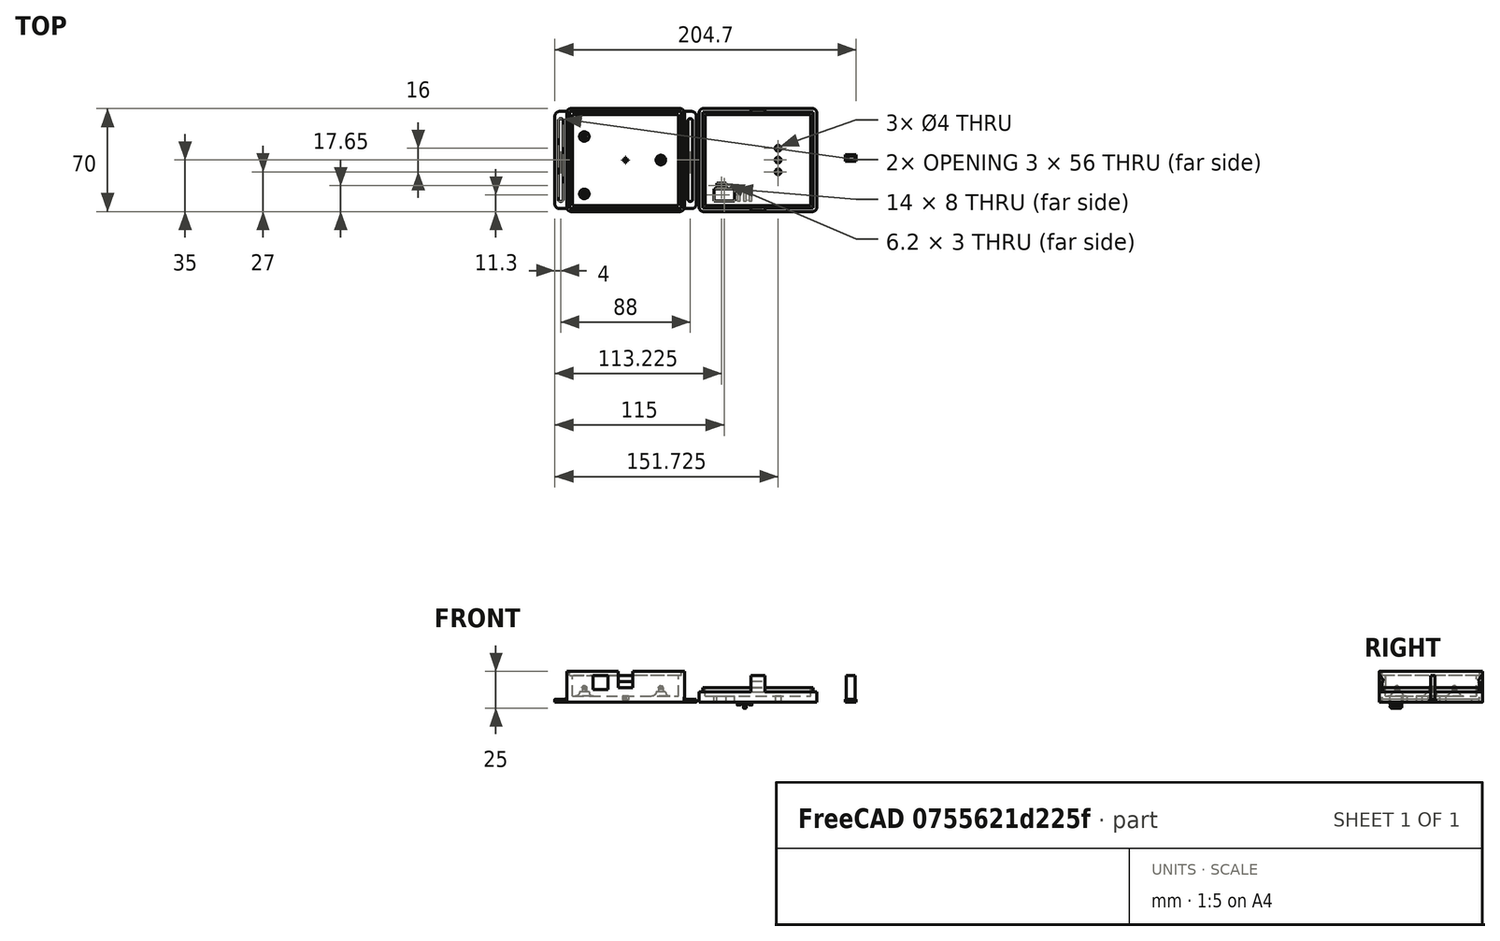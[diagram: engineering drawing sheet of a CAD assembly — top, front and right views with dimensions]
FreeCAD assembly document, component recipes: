
FREECAD ASSEMBLY — COMPONENT RECIPES ("case")

This assembly document has 3 components, labeled P0..P2 below (a component is one placed body or linked part). 3 of them carry a construction recipe — the FreeCAD feature program that regenerates the part from scratch, quoted from this document or its linked companion documents; the rest are supplied as boundary geometry only. No exploded tour is included for this assembly.
COMPONENT P0 — recipe-attached ("bottom_b001", modeled in this document).
Construction recipe (the document's own serialized feature program — sketch geometry with constraints, then the solid features built on it; lengths are millimeters unless a unit is written):

FEATURE [Sketcher::SketchObject] Sketch
  ArcFitTolerance = 1e-06
  AttachmentSupport = -> [XY_Plane001]
  FullyConstrained = true
  MakeInternals = false
  MapMode = 5
  sketch-geometry (4):
    g0: LineSegment StartX=-40 StartY=35 StartZ=0 EndX=-40 EndY=-35 EndZ=0
    g1: LineSegment StartX=-40 StartY=-35 StartZ=0 EndX=40 EndY=-35 EndZ=0
    g2: LineSegment StartX=40 StartY=-35 StartZ=0 EndX=40 EndY=35 EndZ=0
    g3: LineSegment StartX=40 StartY=35 StartZ=0 EndX=-40 EndY=35 EndZ=0
  constraints (10):
    c: Coincident(g0,g1)
    c: Coincident(g1,g2)
    c: Coincident(g2,g3)
    c: Coincident(g3,g0)
    c: Vertical(g2)
    c: Horizontal(g1)
    c: Symmetric(g0,g2,g-2)
    c: Symmetric(g0,g0,g-1)
    c: DistanceX(g3,g3) = 80
    c: DistanceY(g2,g2) = 70
FEATURE [PartDesign::Pad] Pad  label="case"
  Direction = (0,0,1)
  Length = 21
  Length2 = 10
  Profile = -> Sketch
  ReferenceAxis = -> Sketch [N_Axis]
  Refine = true
  Suppressed = false
  Type = 0
FEATURE [PartDesign::Thickness] Thickness  label="case_t"
  Base = -> Pad [Face6]
  BaseFeature = -> Pad
  Intersection = false
  Join = 0
  Mode = 0
  Refine = true
  Reversed = true
  SupportTransform = false
  Suppressed = false
  Value = 4
FEATURE [PartDesign::Fillet] Fillet
  Base = -> Thickness [Edge1,Edge2,Edge5,Edge8]
  BaseFeature = -> Thickness
  Radius = 3
  Refine = true
  SupportTransform = false
  Suppressed = false
  UseAllEdges = false
FEATURE [Sketcher::SketchObject] Sketch001  label="pcb_holders_s"
  ArcFitTolerance = 1e-06
  AttachmentSupport = -> [Fillet]
  FullyConstrained = true
  MakeInternals = false
  MapMode = 5
  Placement = pos=(0,0,4) rot=(0,0,1;0rad)
  sketch-geometry (7):
    g0: Circle CenterX=-28 CenterY=-23 CenterZ=0 NormalX=0 NormalY=0 NormalZ=1 AngleXU=0 Radius=3.25
    g1: Circle CenterX=-28 CenterY=16 CenterZ=0 NormalX=0 NormalY=0 NormalZ=1 AngleXU=0 Radius=3.25
    g2: Circle CenterX=24 CenterY=-1.1e-15 CenterZ=0 NormalX=0 NormalY=0 NormalZ=1 AngleXU=0 Radius=3.25
    g3: LineSegment [constr] StartX=-32 StartY=27 StartZ=0 EndX=-32 EndY=-27 EndZ=0
    g4: LineSegment [constr] StartX=-32 StartY=-27 StartZ=0 EndX=32 EndY=-27 EndZ=0
    g5: LineSegment [constr] StartX=32 StartY=-27 StartZ=0 EndX=32 EndY=27 EndZ=0
    g6: LineSegment [constr] StartX=32 StartY=27 StartZ=0 EndX=-32 EndY=27 EndZ=0
  constraints (19):
    c: Radius(g0) = 3.25
    c: Radius(g1) = 3.25
    c: Diameter(g2) = 6.5
    c: Coincident(g3,g4)
    c: Coincident(g4,g5)
    c: Coincident(g5,g6)
    c: Coincident(g6,g3)
    c: Vertical(g3)
    c: Horizontal(g6)
    c: DistanceX(g6,g6) = 64
    c: DistanceY(g3,g3) = 54
    c: Symmetric(g3,g4,g-2)
    c: Symmetric(g5,g4,g-1)
    c: Distance(g0,g4) = 4
    c: Distance(g0,g3) = 4
    c: Distance(g1,g3) = 4
    c: Distance(g1,g6) = 11
    c: Distance(g2,g5) = 8
    c: Distance(g2,g4) = 27
FEATURE [PartDesign::Pad] Pad001  label="pcb_holders_p"
  BaseFeature = -> Fillet
  Direction = (0,0,1)
  Length = 3
  Length2 = 10
  Profile = -> Sketch001
  ReferenceAxis = -> Sketch001 [N_Axis]
  Refine = true
  Suppressed = false
  Type = 0
FEATURE [PartDesign::Fillet] Fillet001  label="pcb_holder_f"
  Base = -> Pad001 [Edge39,Edge38,Edge37]
  BaseFeature = -> Pad001
  Radius = 2.99
  Refine = true
  SupportTransform = false
  Suppressed = false
  UseAllEdges = false
FEATURE [Sketcher::SketchObject] Sketch003  label="barreljack_window_s"
  ArcFitTolerance = 1e-06
  AttachmentOffset = pos=(0,0,8.55) rot=(0,0,1;0rad)
  AttachmentSupport = -> [XY_Plane001]
  FullyConstrained = true
  MakeInternals = false
  MapMode = 5
  Placement = pos=(0,0,8.55) rot=(0,0,1;0rad)
  sketch-geometry (8):
    g0: LineSegment [constr] StartX=-32 StartY=27 StartZ=0 EndX=-32 EndY=-27 EndZ=0
    g1: LineSegment [constr] StartX=-32 StartY=-27 StartZ=0 EndX=32 EndY=-27 EndZ=0
    g2: LineSegment [constr] StartX=32 StartY=-27 StartZ=0 EndX=32 EndY=27 EndZ=0
    g3: LineSegment [constr] StartX=32 StartY=27 StartZ=0 EndX=-32 EndY=27 EndZ=0
    g4: LineSegment StartX=-22 StartY=-20 StartZ=0 EndX=-22 EndY=-36 EndZ=0
    g5: LineSegment StartX=-22 StartY=-36 StartZ=0 EndX=-12 EndY=-36 EndZ=0
    g6: LineSegment StartX=-12 StartY=-36 StartZ=0 EndX=-12 EndY=-20 EndZ=0
    g7: LineSegment StartX=-12 StartY=-20 StartZ=0 EndX=-22 EndY=-20 EndZ=0
  constraints (22):
    c: Coincident(g0,g1)
    c: Coincident(g1,g2)
    c: Coincident(g2,g3)
    c: Coincident(g3,g0)
    c: Vertical(g2)
    c: Horizontal(g1)
    c: Distance(g0,g2) = 64
    c: Distance(g1,g3) = 54
    c: Symmetric(g0,g2,g-2)
    c: Symmetric(g0,g0,g-1)
    c: Coincident(g4,g5)
    c: Coincident(g5,g6)
    c: Coincident(g6,g7)
    c: Coincident(g7,g4)
    c: Vertical(g4)
    c: Vertical(g6)
    c: Horizontal(g5)
    c: Horizontal(g7)
    c: Distance(g0,g4) = 10
    c: DistanceX(g7,g7) = 10
    c: DistanceY(g6,g6) = 16
    c: Distance(g1,g7) = 7
FEATURE [PartDesign::Pocket] Pocket  label="barreljack_window_p"
  BaseFeature = -> Fillet001
  Direction = (0,0,-1)
  Length = 9.5
  Length2 = 5
  Profile = -> Sketch003
  ReferenceAxis = -> Sketch003 [N_Axis]
  Refine = true
  Reversed = true
  Suppressed = false
  Type = 0
FEATURE [Sketcher::SketchObject] Sketch004  label="fitting_s001"
  ArcFitTolerance = 1e-06
  AttachmentOffset = pos=(0,0,18) rot=(0,0,1;0rad)
  AttachmentSupport = -> [XY_Plane001]
  ExternalGeometry = -> [Pocket]
  FullyConstrained = true
  MakeInternals = false
  MapMode = 5
  Placement = pos=(0,0,18) rot=(0,0,1;0rad)
  sketch-geometry (4):
    g0: LineSegment StartX=-38 StartY=33 StartZ=0 EndX=-38 EndY=-33 EndZ=0
    g1: LineSegment StartX=-38 StartY=-33 StartZ=0 EndX=38 EndY=-33 EndZ=0
    g2: LineSegment StartX=38 StartY=-33 StartZ=0 EndX=38 EndY=33 EndZ=0
    g3: LineSegment StartX=38 StartY=33 StartZ=0 EndX=-38 EndY=33 EndZ=0
  constraints (12):
    c: Coincident(g0,g1)
    c: Coincident(g1,g2)
    c: Coincident(g2,g3)
    c: Coincident(g3,g0)
    c: Vertical(g0)
    c: Vertical(g2)
    c: Horizontal(g1)
    c: Horizontal(g3)
    c: DistanceX(g0,g-4) = 2
    c: DistanceY(g-4,g0) = 2
    c: DistanceY(g1,g-6) = 2
    c: DistanceX(g-6,g1) = 2
FEATURE [PartDesign::Pocket] Pocket001  label="fitting_p001"
  BaseFeature = -> Pocket
  Direction = (0,0,-1)
  Length = 5
  Length2 = 5
  Profile = -> Sketch004
  ReferenceAxis = -> Sketch004 [N_Axis]
  Refine = true
  Reversed = true
  Suppressed = false
  Type = 0
FEATURE [Sketcher::SketchObject] Sketch018  label="holders_s"
  ArcFitTolerance = 1e-06
  AttachmentSupport = -> [XY_Plane001]
  FullyConstrained = true
  MakeInternals = false
  MapMode = 5
  sketch-geometry (40):
    g0: LineSegment StartX=-38 StartY=33 StartZ=0 EndX=-45 EndY=33 EndZ=0
    g1: LineSegment StartX=-48 StartY=30 StartZ=0 EndX=-48 EndY=-30 EndZ=0
    g2: LineSegment StartX=-45 StartY=-33 StartZ=0 EndX=-38 EndY=-33 EndZ=0
    g3: LineSegment StartX=-38 StartY=-33 StartZ=0 EndX=-38 EndY=33 EndZ=0
    g4: LineSegment StartX=38 StartY=33 StartZ=0 EndX=38 EndY=-33 EndZ=0
    g5: LineSegment StartX=38 StartY=-33 StartZ=0 EndX=45 EndY=-33 EndZ=0
    g6: LineSegment StartX=48 StartY=-30 StartZ=0 EndX=48 EndY=30 EndZ=0
    g7: LineSegment StartX=45 StartY=33 StartZ=0 EndX=38 EndY=33 EndZ=0
    g8: ArcOfCircle CenterX=-45 CenterY=30 CenterZ=0 NormalX=0 NormalY=0 NormalZ=1 AngleXU=0 Radius=3 StartAngle=1.5708 EndAngle=3.14159
    g9: GeomPoint [constr] X=-48 Y=33 Z=0
    g10: ArcOfCircle CenterX=-45 CenterY=-30 CenterZ=0 NormalX=0 NormalY=0 NormalZ=1 AngleXU=0 Radius=3 StartAngle=3.14159 EndAngle=4.71239
    g11: GeomPoint [constr] X=-48 Y=-33 Z=0
    g12: ArcOfCircle CenterX=45 CenterY=30 CenterZ=0 NormalX=0 NormalY=0 NormalZ=1 AngleXU=0 Radius=3 StartAngle=2e-16 EndAngle=1.5708
    g13: GeomPoint [constr] X=48 Y=33 Z=0
    g14: ArcOfCircle CenterX=45 CenterY=-30 CenterZ=0 NormalX=0 NormalY=0 NormalZ=1 AngleXU=0 Radius=3 StartAngle=4.71239 EndAngle=6.28319
    g15: GeomPoint [constr] X=48 Y=-33 Z=0
    g16: LineSegment StartX=-45.5 StartY=27 StartZ=0 EndX=-45.5 EndY=-27 EndZ=0
    g17: LineSegment StartX=-44.5 StartY=-28 StartZ=0 EndX=-43.5 EndY=-28 EndZ=0
    g18: LineSegment StartX=-42.5 StartY=-27 StartZ=0 EndX=-42.5 EndY=27 EndZ=0
    g19: LineSegment StartX=-43.5 StartY=28 StartZ=0 EndX=-44.5 EndY=28 EndZ=0
    g20: LineSegment StartX=42.5 StartY=27 StartZ=0 EndX=42.5 EndY=-27 EndZ=0
    g21: LineSegment StartX=43.5 StartY=-28 StartZ=0 EndX=44.5 EndY=-28 EndZ=0
    g22: LineSegment StartX=45.5 StartY=-27 StartZ=0 EndX=45.5 EndY=27 EndZ=0
    g23: LineSegment StartX=44.5 StartY=28 StartZ=0 EndX=43.5 EndY=28 EndZ=0
    g24: ArcOfCircle CenterX=-44.5 CenterY=27 CenterZ=0 NormalX=0 NormalY=0 NormalZ=1 AngleXU=0 Radius=1 StartAngle=1.5708 EndAngle=3.14159
    g25: GeomPoint [constr] X=-45.5 Y=28 Z=0
    g26: ArcOfCircle CenterX=-43.5 CenterY=27 CenterZ=0 NormalX=0 NormalY=0 NormalZ=1 AngleXU=0 Radius=1 StartAngle=1.7e-15 EndAngle=1.5708
    g27: GeomPoint [constr] X=-42.5 Y=28 Z=0
    g28: ArcOfCircle CenterX=-44.5 CenterY=-27 CenterZ=0 NormalX=0 NormalY=0 NormalZ=1 AngleXU=0 Radius=1 StartAngle=3.14159 EndAngle=4.71239
    g29: GeomPoint [constr] X=-45.5 Y=-28 Z=0
    g30: ArcOfCircle CenterX=-43.5 CenterY=-27 CenterZ=0 NormalX=0 NormalY=0 NormalZ=1 AngleXU=0 Radius=1 StartAngle=4.71239 EndAngle=6.28319
    g31: GeomPoint [constr] X=-42.5 Y=-28 Z=0
    g32: ArcOfCircle CenterX=43.5 CenterY=-27 CenterZ=0 NormalX=0 NormalY=0 NormalZ=1 AngleXU=0 Radius=1 StartAngle=3.14159 EndAngle=4.71239
    g33: GeomPoint [constr] X=42.5 Y=-28 Z=0
    g34: ArcOfCircle CenterX=44.5 CenterY=-27 CenterZ=0 NormalX=0 NormalY=0 NormalZ=1 AngleXU=0 Radius=1 StartAngle=4.71239 EndAngle=6.28319
    g35: GeomPoint [constr] X=45.5 Y=-28 Z=0
    g36: ArcOfCircle CenterX=43.5 CenterY=27 CenterZ=0 NormalX=0 NormalY=0 NormalZ=1 AngleXU=0 Radius=1 StartAngle=1.5708 EndAngle=3.14159
    g37: GeomPoint [constr] X=42.5 Y=28 Z=0
    g38: ArcOfCircle CenterX=44.5 CenterY=27 CenterZ=0 NormalX=0 NormalY=0 NormalZ=1 AngleXU=0 Radius=1 StartAngle=-5.7785e-12 EndAngle=1.5708
    g39: GeomPoint [constr] X=45.5 Y=28 Z=0
  constraints (94):
    c: Coincident(g2,g3)
    c: Coincident(g3,g0)
    c: Horizontal(g0)
    c: Horizontal(g2)
    c: Vertical(g1)
    c: Vertical(g3)
    c: Distance(g9,g3) = 10
    c: Distance(g0,g2) = 66
    c: Coincident(g0,g-3)
    c: Coincident(g4,g5)
    c: Coincident(g7,g4)
    c: Vertical(g4)
    c: Vertical(g6)
    c: Horizontal(g5)
    c: Horizontal(g7)
    c: Distance(g4,g13) = 10
    c: Distance(g5,g7) = 66
    c: Coincident(g4,g-4)
    c: PointOnObject(g9,g0)
    c: PointOnObject(g9,g1)
    c: Tangent(g0,g8) = -1.5708
    c: Tangent(g1,g8) = -1.5708
    c: PointOnObject(g11,g1)
    c: PointOnObject(g11,g2)
    c: Tangent(g1,g10) = -1.5708
    c: Tangent(g2,g10) = -1.5708
    c: PointOnObject(g13,g7)
    c: PointOnObject(g13,g6)
    c: Tangent(g7,g12) = -1.5708
    c: Tangent(g6,g12) = -1.5708
    c: PointOnObject(g15,g5)
    c: PointOnObject(g15,g6)
    c: Tangent(g5,g14) = -1.5708
    c: Tangent(g6,g14) = -1.5708
    c: Radius(g8) = 3
    c: Radius(g10) = 3
    c: Radius(g14) = 3
    c: Radius(g12) = 3
    c: Vertical(g16)
    c: Vertical(g18)
    c: Horizontal(g17)
    c: Horizontal(g19)
    c: Distance(g25,g27) = 3
    c: Distance(g29,g25) = 56
    c: Distance(g3,g18) = 4.5
    c: Vertical(g20)
    c: Vertical(g22)
    c: Horizontal(g21)
    c: Horizontal(g23)
    c: Distance(g37,g39) = 3
    c: Distance(g33,g37) = 56
    c: Distance(g4,g20) = 4.5
    c: Distance(g27,g0) = 5
    c: Distance(g39,g7) = 5
    c: PointOnObject(g25,g19)
    c: PointOnObject(g25,g16)
    c: Tangent(g19,g24) = -1.5708
    c: Tangent(g16,g24) = -1.5708
    c: PointOnObject(g27,g19)
    c: PointOnObject(g27,g18)
    c: Tangent(g19,g26) = -1.5708
    c: Tangent(g18,g26) = -1.5708
    c: PointOnObject(g29,g17)
    c: PointOnObject(g29,g16)
    c: Tangent(g17,g28) = -1.5708
    c: Tangent(g16,g28) = -1.5708
    c: PointOnObject(g31,g17)
    c: PointOnObject(g31,g18)
    c: Tangent(g17,g30) = -1.5708
    c: Tangent(g18,g30) = -1.5708
    c: PointOnObject(g33,g20)
    c: PointOnObject(g33,g21)
    c: Tangent(g20,g32) = -1.5708
    c: Tangent(g21,g32) = -1.5708
    c: PointOnObject(g35,g22)
    c: PointOnObject(g35,g21)
    c: Tangent(g22,g34) = -1.5708
    c: Tangent(g21,g34) = -1.5708
    c: PointOnObject(g37,g23)
    c: PointOnObject(g37,g20)
    c: Tangent(g23,g36) = -1.5708
    c: Tangent(g20,g36) = -1.5708
    c: PointOnObject(g39,g23)
    c: PointOnObject(g39,g22)
    c: Tangent(g23,g38) = -1.5708
    c: Tangent(g22,g38) = -1.5708
    c: Radius(g24) = 1
    c: Radius(g26) = 1
    c: Radius(g28) = 1
    c: Radius(g30) = 1
    c: Radius(g32) = 1
    c: Radius(g34) = 1
    c: Radius(g36) = 1
    c: Radius(g38) = 1
FEATURE [PartDesign::Pad] Pad009  label="holders_p"
  BaseFeature = -> Pocket001
  Direction = (0,0,1)
  Length = 2
  Length2 = 10
  Profile = -> Sketch018
  ReferenceAxis = -> Sketch018 [N_Axis]
  Refine = true
  Suppressed = false
  Type = 0
FEATURE [PartDesign::Fillet] Fillet004  label="holders_f"
  Base = -> Pad009 [Edge77,Edge89]
  BaseFeature = -> Pad009
  Radius = 1.5
  Refine = true
  SupportTransform = false
  Suppressed = false
  UseAllEdges = false
FEATURE [Sketcher::SketchObject] Sketch016  label="clips_holders_s"
  ArcFitTolerance = 1e-06
  AttachmentSupport = -> [YZ_Plane001]
  ExternalGeometry = -> [Pad]
  FullyConstrained = true
  MakeInternals = false
  MapMode = 5
  Placement = pos=(0,0,0) rot=(0.57735,0.57735,0.57735;2.0944rad)
  sketch-geometry (10):
    g0: LineSegment StartX=33 StartY=18 StartZ=0 EndX=35 EndY=18 EndZ=0
    g1: LineSegment StartX=35 StartY=18 StartZ=0 EndX=35 EndY=9.9 EndZ=0
    g2: LineSegment StartX=35 StartY=9.9 StartZ=0 EndX=31.9 EndY=14.1 EndZ=0
    g3: LineSegment StartX=31.9 StartY=14.1 StartZ=0 EndX=33 EndY=14.1 EndZ=0
    g4: LineSegment StartX=33 StartY=14.1 StartZ=0 EndX=33 EndY=18 EndZ=0
    g5: LineSegment StartX=-33 StartY=18 StartZ=0 EndX=-35 EndY=18 EndZ=0
    g6: LineSegment StartX=-35 StartY=18 StartZ=0 EndX=-35 EndY=9.9 EndZ=0
    g7: LineSegment StartX=-35 StartY=9.9 StartZ=0 EndX=-31.9 EndY=14.1 EndZ=0
    g8: LineSegment StartX=-31.9 StartY=14.1 StartZ=0 EndX=-33 EndY=14.1 EndZ=0
    g9: LineSegment StartX=-33 StartY=14.1 StartZ=0 EndX=-33 EndY=18 EndZ=0
  constraints (30):
    c: Coincident(g0,g1)
    c: Vertical(g1)
    c: Coincident(g2,g3)
    c: Coincident(g3,g4)
    c: Coincident(g4,g0)
    c: Vertical(g4)
    c: Coincident(g7,g8)
    c: Coincident(g8,g9)
    c: Coincident(g9,g5)
    c: Horizontal(g5)
    c: Coincident(g6,g5)
    c: DistanceY(g6,g6) = 8.1
    c: DistanceY(g9,g9) = 3.9
    c: Vertical(g9)
    c: Horizontal(g8)
    c: Vertical(g6)
    c: DistanceX(g8,g8) = 1.1
    c: DistanceY(g1,g1) = 8.1
    c: Horizontal(g3)
    c: DistanceX(g0,g0) = 2
    c: DistanceY(g4,g4) = 3.9
    c: DistanceX(g3,g3) = 1.1
    c: Horizontal(g0)
    c: DistanceX(g5,g5) = 2
    c: DistanceY(g5,g-3) = 3
    c: PointOnObject(g5,g-4)
    c: DistanceY(g0,g-5) = 3
    c: PointOnObject(g0,g-5)
    c: Coincident(g2,g1)
    c: Coincident(g7,g6)
FEATURE [PartDesign::Pocket] Pocket007  label="clip_holders_p"
  BaseFeature = -> Fillet004
  Direction = (-1,0,0)
  Length = 10
  Length2 = 5
  Midplane = true
  Profile = -> Sketch016
  ReferenceAxis = -> Sketch016 [N_Axis]
  Refine = true
  Suppressed = false
  Type = 0
FEATURE [Sketcher::SketchObject] Sketch019  label="clip_holders_clearance_s"
  ArcFitTolerance = 1e-06
  AttachmentSupport = -> [YZ_Plane001]
  ExternalGeometry = -> [Pocket007]
  FullyConstrained = true
  MakeInternals = false
  MapMode = 5
  Placement = pos=(0,0,0) rot=(0.57735,0.57735,0.57735;2.0944rad)
  sketch-geometry (8):
    g0: LineSegment StartX=-33 StartY=21 StartZ=0 EndX=-35 EndY=21 EndZ=0
    g1: LineSegment StartX=-35 StartY=21 StartZ=0 EndX=-35 EndY=18 EndZ=0
    g2: LineSegment StartX=-35 StartY=18 StartZ=0 EndX=-33 EndY=18 EndZ=0
    g3: LineSegment StartX=-33 StartY=18 StartZ=0 EndX=-33 EndY=21 EndZ=0
    g4: LineSegment StartX=33 StartY=21 StartZ=0 EndX=33 EndY=18 EndZ=0
    g5: LineSegment StartX=33 StartY=18 StartZ=0 EndX=35 EndY=18 EndZ=0
    g6: LineSegment StartX=35 StartY=18 StartZ=0 EndX=35 EndY=21 EndZ=0
    g7: LineSegment StartX=35 StartY=21 StartZ=0 EndX=33 EndY=21 EndZ=0
  constraints (20):
    c: Coincident(g0,g1)
    c: Coincident(g1,g2)
    c: Coincident(g2,g3)
    c: Coincident(g3,g0)
    c: Horizontal(g0)
    c: Horizontal(g2)
    c: Vertical(g1)
    c: Vertical(g3)
    c: Coincident(g0,g-5)
    c: Coincident(g1,g-6)
    c: Coincident(g4,g5)
    c: Coincident(g5,g6)
    c: Coincident(g6,g7)
    c: Coincident(g7,g4)
    c: Vertical(g4)
    c: Vertical(g6)
    c: Horizontal(g5)
    c: Horizontal(g7)
    c: Coincident(g4,g-10)
    c: Coincident(g5,g-9)
FEATURE [PartDesign::Pocket] Pocket008  label="clip_holder_clearance_p"
  BaseFeature = -> Pocket007
  Direction = (-1,0,0)
  Length = 10
  Length2 = 5
  Midplane = true
  Profile = -> Sketch019
  ReferenceAxis = -> Sketch019 [N_Axis]
  Refine = true
  Suppressed = false
  Type = 0
FEATURE [PartDesign::Boolean] Boolean006
  BaseFeature = -> Pocket008
  Group = -> [Body005]
  Refine = true
  Suppressed = false
  Type = 0
  UsePlacement = true
FEATURE [PartDesign::Boolean] Boolean007
  BaseFeature = -> Boolean006
  Group = -> [Body008,Body011]
  Refine = true
  Suppressed = false
  Type = 0
  UsePlacement = true
FEATURE [PartDesign::Body] Body  label="bottom_b"
  AllowCompound = false
  Group = -> [Sketch,Pad,Thickness,Fillet,Sketch001,Pad001,Fillet001,Sketch003,Pocket,Sketch004,Pocket001,Sketch016,Sketch018,Pad009,Fillet004,Pocket007,Sketch019,Pocket008,Boolean006,Boolean007]
  Origin = -> Origin001
  Tip = -> Boolean007
COMPONENT P1 — recipe-attached ("button_b001", modeled in this document).
Construction recipe (the document's own serialized feature program — sketch geometry with constraints, then the solid features built on it; lengths are millimeters unless a unit is written):

FEATURE [Sketcher::SketchObject] Sketch014
  ArcFitTolerance = 1e-06
  AttachmentSupport = -> [XY_Plane005]
  FullyConstrained = true
  MakeInternals = false
  MapMode = 5
  sketch-geometry (4):
    g0: LineSegment StartX=0 StartY=2.7 StartZ=0 EndX=0 EndY=0 EndZ=0
    g1: LineSegment StartX=0 StartY=0 StartZ=0 EndX=5.9 EndY=0 EndZ=0
    g2: LineSegment StartX=5.9 StartY=0 StartZ=0 EndX=5.9 EndY=2.7 EndZ=0
    g3: LineSegment StartX=5.9 StartY=2.7 StartZ=0 EndX=0 EndY=2.7 EndZ=0
  constraints (11):
    c: Coincident(g0,g1)
    c: Coincident(g1,g2)
    c: Coincident(g2,g3)
    c: Coincident(g3,g0)
    c: Vertical(g0)
    c: Vertical(g2)
    c: Horizontal(g1)
    c: Horizontal(g3)
    c: Distance(g0,g2) = 5.9
    c: Distance(g1,g3) = 2.7
    c: Coincident(g0,g-1)
FEATURE [PartDesign::Pad] Pad006
  Direction = (0,0,1)
  Length = 18
  Length2 = 10
  Profile = -> Sketch014
  ReferenceAxis = -> Sketch014 [N_Axis]
  Refine = true
  Suppressed = false
  Type = 0
FEATURE [Sketcher::SketchObject] Sketch015
  ArcFitTolerance = 1e-06
  AttachmentSupport = -> [XY_Plane005]
  ExternalGeometry = -> [Sketch014]
  FullyConstrained = true
  MakeInternals = false
  MapMode = 5
  sketch-geometry (4):
    g0: LineSegment StartX=-0.8 StartY=3.5 StartZ=0 EndX=-0.8 EndY=-0.8 EndZ=0
    g1: LineSegment StartX=-0.8 StartY=-0.8 StartZ=0 EndX=6.7 EndY=-0.8 EndZ=0
    g2: LineSegment StartX=6.7 StartY=-0.8 StartZ=0 EndX=6.7 EndY=3.5 EndZ=0
    g3: LineSegment StartX=6.7 StartY=3.5 StartZ=0 EndX=-0.8 EndY=3.5 EndZ=0
  constraints (12):
    c: Coincident(g0,g1)
    c: Coincident(g1,g2)
    c: Coincident(g2,g3)
    c: Coincident(g3,g0)
    c: Vertical(g0)
    c: Vertical(g2)
    c: Horizontal(g1)
    c: Horizontal(g3)
    c: Distance(g-3,g3) = 0.8
    c: Distance(g2,g-4) = 0.8
    c: Distance(g-3,g0) = 0.8
    c: Distance(g-4,g1) = 0.8
FEATURE [PartDesign::Pad] Pad007
  BaseFeature = -> Pad006
  Direction = (0,0,1)
  Length = 2
  Length2 = 10
  Profile = -> Sketch015
  ReferenceAxis = -> Sketch015 [N_Axis]
  Refine = true
  Suppressed = false
  Type = 0
FEATURE [PartDesign::Body] Body004  label="button_b"
  AllowCompound = false
  Group = -> [Sketch014,Pad006,Sketch015,Pad007]
  Origin = -> Origin005
  Placement = pos=(150,0,0) rot=(0,0,1;0rad)
  Tip = -> Pad007
COMPONENT P2 — recipe-attached ("top_b001", modeled in this document).
Construction recipe (the document's own serialized feature program — sketch geometry with constraints, then the solid features built on it; lengths are millimeters unless a unit is written):

FEATURE [Sketcher::SketchObject] Sketch005  label="case_s"
  ArcFitTolerance = 1e-06
  AttachmentSupport = -> [XY_Plane002]
  FullyConstrained = true
  MakeInternals = false
  MapMode = 5
  sketch-geometry (4):
    g0: LineSegment StartX=-40 StartY=35 StartZ=0 EndX=-40 EndY=-35 EndZ=0
    g1: LineSegment StartX=-40 StartY=-35 StartZ=0 EndX=40 EndY=-35 EndZ=0
    g2: LineSegment StartX=40 StartY=-35 StartZ=0 EndX=40 EndY=35 EndZ=0
    g3: LineSegment StartX=40 StartY=35 StartZ=0 EndX=-40 EndY=35 EndZ=0
  constraints (10):
    c: Coincident(g0,g1)
    c: Coincident(g1,g2)
    c: Coincident(g2,g3)
    c: Coincident(g3,g0)
    c: Vertical(g2)
    c: Horizontal(g1)
    c: Symmetric(g0,g2,g-2)
    c: Symmetric(g0,g0,g-1)
    c: DistanceX(g3,g3) = 80
    c: DistanceY(g2,g2) = 70
FEATURE [PartDesign::Pad] Pad003  label="case_p"
  Direction = (0,0,1)
  Length = 10
  Length2 = 10
  Profile = -> Sketch005
  ReferenceAxis = -> Sketch005 [N_Axis]
  Refine = true
  Suppressed = false
  Type = 0
FEATURE [PartDesign::Thickness] Thickness001  label="case_t001"
  Base = -> Pad003 [Face6]
  BaseFeature = -> Pad003
  Intersection = false
  Join = 0
  Mode = 0
  Refine = true
  Reversed = true
  SupportTransform = false
  Suppressed = false
  Value = 4
FEATURE [PartDesign::Fillet] Fillet002
  Base = -> Thickness001 [Edge2,Edge1,Edge5,Edge8]
  BaseFeature = -> Thickness001
  Radius = 3
  Refine = true
  SupportTransform = false
  Suppressed = false
  UseAllEdges = false
FEATURE [Sketcher::SketchObject] Sketch008  label="fitting_s"
  ArcFitTolerance = 1e-06
  AttachmentOffset = pos=(0,0,7) rot=(0,0,1;0rad)
  AttachmentSupport = -> [XY_Plane002]
  FullyConstrained = true
  MakeInternals = false
  MapMode = 5
  Placement = pos=(0,0,7) rot=(0,0,1;0rad)
  sketch-geometry (20):
    g0: LineSegment StartX=-42.5 StartY=50 StartZ=0 EndX=-42.5 EndY=-50 EndZ=0
    g1: LineSegment StartX=-42.5 StartY=-50 StartZ=0 EndX=-37.5 EndY=-50 EndZ=0
    g2: LineSegment StartX=-37.5 StartY=-50 StartZ=0 EndX=-37.5 EndY=50 EndZ=0
    g3: LineSegment StartX=-37.5 StartY=50 StartZ=0 EndX=-42.5 EndY=50 EndZ=0
    g4: LineSegment StartX=-50 StartY=37.5 StartZ=0 EndX=-50 EndY=32.5 EndZ=0
    g5: LineSegment StartX=-50 StartY=32.5 StartZ=0 EndX=50 EndY=32.5 EndZ=0
    g6: LineSegment StartX=50 StartY=32.5 StartZ=0 EndX=50 EndY=37.5 EndZ=0
    g7: LineSegment StartX=50 StartY=37.5 StartZ=0 EndX=-50 EndY=37.5 EndZ=0
    g8: LineSegment StartX=37.5 StartY=50 StartZ=0 EndX=37.5 EndY=-50 EndZ=0
    g9: LineSegment StartX=37.5 StartY=-50 StartZ=0 EndX=42.5 EndY=-50 EndZ=0
    g10: LineSegment StartX=42.5 StartY=-50 StartZ=0 EndX=42.5 EndY=50 EndZ=0
    g11: LineSegment StartX=42.5 StartY=50 StartZ=0 EndX=37.5 EndY=50 EndZ=0
    g12: LineSegment StartX=50 StartY=-37.5 StartZ=0 EndX=50 EndY=-32.5 EndZ=0
    g13: LineSegment StartX=50 StartY=-32.5 StartZ=0 EndX=-50 EndY=-32.5 EndZ=0
    g14: LineSegment StartX=-50 StartY=-32.5 StartZ=0 EndX=-50 EndY=-37.5 EndZ=0
    g15: LineSegment StartX=-50 StartY=-37.5 StartZ=0 EndX=50 EndY=-37.5 EndZ=0
    g16: LineSegment [constr] StartX=-40 StartY=35 StartZ=0 EndX=-40 EndY=-35 EndZ=0
    g17: LineSegment [constr] StartX=-40 StartY=-35 StartZ=0 EndX=40 EndY=-35 EndZ=0
    g18: LineSegment [constr] StartX=40 StartY=-35 StartZ=0 EndX=40 EndY=35 EndZ=0
    g19: LineSegment [constr] StartX=40 StartY=35 StartZ=0 EndX=-40 EndY=35 EndZ=0
  constraints (54):
    c: Coincident(g0,g1)
    c: Coincident(g1,g2)
    c: Coincident(g2,g3)
    c: Coincident(g3,g0)
    c: Vertical(g2)
    c: Horizontal(g1)
    c: Horizontal(g3)
    c: Coincident(g4,g5)
    c: Coincident(g5,g6)
    c: Coincident(g6,g7)
    c: Coincident(g7,g4)
    c: Vertical(g4)
    c: Vertical(g6)
    c: Horizontal(g5)
    c: Coincident(g8,g9)
    c: Coincident(g9,g10)
    c: Coincident(g10,g11)
    c: Coincident(g11,g8)
    c: Vertical(g8)
    c: Horizontal(g9)
    c: Horizontal(g11)
    c: Coincident(g12,g13)
    c: Coincident(g13,g14)
    c: Coincident(g14,g15)
    c: Coincident(g15,g12)
    c: Vertical(g12)
    c: Vertical(g14)
    c: Horizontal(g15)
    c: DistanceY(g14,g14) = 5
    c: DistanceX(g9,g9) = 5
    c: DistanceY(g6,g6) = 5
    c: DistanceX(g1,g1) = 5
    c: Symmetric(g0,g0,g-1)
    c: Symmetric(g10,g9,g-1)
    c: Symmetric(g13,g12,g-2)
    c: Symmetric(g4,g6,g-2)
    c: DistanceX(g7,g7) = 100
    c: DistanceY(g0,g0) = 100
    c: DistanceY(g10,g10) = 100
    c: DistanceX(g15,g15) = 100
    c: Coincident(g16,g17)
    c: Coincident(g17,g18)
    c: Coincident(g18,g19)
    c: Coincident(g19,g16)
    c: Vertical(g18)
    c: Horizontal(g19)
    c: Distance(g16,g18) = 80
    c: Distance(g17,g19) = 70
    c: Symmetric(g16,g16,g-1)
    c: Symmetric(g16,g17,g-2)
    c: DistanceX(g16,g2) = 2.5
    c: DistanceX(g8,g18) = 2.5
    c: DistanceY(g4,g16) = 2.5
    c: DistanceY(g16,g13) = 2.5
FEATURE [PartDesign::Pocket] Pocket002  label="fitting_p"
  BaseFeature = -> Fillet002
  Direction = (0,0,-1)
  Length = 5
  Length2 = 5
  Profile = -> Sketch008
  ReferenceAxis = -> Sketch008 [N_Axis]
  Refine = true
  Reversed = true
  Suppressed = false
  Type = 0
FEATURE [Sketcher::SketchObject] Sketch009  label="top_holes_sk"
  ArcFitTolerance = 1e-06
  AttachmentOffset = pos=(0,-1,0) rot=(0,0,1;0rad)
  AttachmentSupport = -> [XY_Plane002]
  FullyConstrained = true
  MakeInternals = false
  MapMode = 5
  Placement = pos=(0,-1,0) rot=(0,0,1;0rad)
  sketch-geometry (15):
    g0: LineSegment [constr] StartX=-32 StartY=27 StartZ=0 EndX=-32 EndY=-27 EndZ=0
    g1: LineSegment [constr] StartX=-32 StartY=-27 StartZ=0 EndX=32 EndY=-27 EndZ=0
    g2: LineSegment [constr] StartX=32 StartY=-27 StartZ=0 EndX=32 EndY=27 EndZ=0
    g3: LineSegment [constr] StartX=32 StartY=27 StartZ=0 EndX=-32 EndY=27 EndZ=0
    g4: LineSegment StartX=-30 StartY=-18.7 StartZ=0 EndX=-30 EndY=-26.7 EndZ=0
    g5: LineSegment StartX=-30 StartY=-26.7 StartZ=0 EndX=-16 EndY=-26.7 EndZ=0
    g6: LineSegment StartX=-16 StartY=-26.7 StartZ=0 EndX=-16 EndY=-18.7 EndZ=0
    g7: LineSegment StartX=-16 StartY=-18.7 StartZ=0 EndX=-30 EndY=-18.7 EndZ=0
    g8: LineSegment StartX=-27.875 StartY=-14.85 StartZ=0 EndX=-27.875 EndY=-17.85 EndZ=0
    g9: LineSegment StartX=-27.875 StartY=-17.85 StartZ=0 EndX=-21.675 EndY=-17.85 EndZ=0
    g10: LineSegment StartX=-21.675 StartY=-17.85 StartZ=0 EndX=-21.675 EndY=-14.85 EndZ=0
    g11: LineSegment StartX=-21.675 StartY=-14.85 StartZ=0 EndX=-27.875 EndY=-14.85 EndZ=0
    g12: Circle CenterX=13.725 CenterY=9 CenterZ=0 NormalX=0 NormalY=0 NormalZ=1 AngleXU=0 Radius=2
    g13: Circle CenterX=13.725 CenterY=1 CenterZ=0 NormalX=0 NormalY=0 NormalZ=1 AngleXU=0 Radius=2
    g14: Circle CenterX=13.725 CenterY=-7 CenterZ=0 NormalX=0 NormalY=0 NormalZ=1 AngleXU=0 Radius=2
  constraints (43):
    c: Coincident(g0,g1)
    c: Coincident(g1,g2)
    c: Coincident(g2,g3)
    c: Coincident(g3,g0)
    c: Vertical(g2)
    c: Horizontal(g1)
    c: Distance(g0,g2) = 64
    c: Distance(g1,g3) = 54
    c: Symmetric(g0,g2,g-2)
    c: Symmetric(g0,g0,g-1)
    c: Coincident(g4,g5)
    c: Coincident(g5,g6)
    c: Coincident(g6,g7)
    c: Coincident(g7,g4)
    c: Vertical(g4)
    c: Vertical(g6)
    c: Horizontal(g5)
    c: Horizontal(g7)
    c: Coincident(g8,g9)
    c: Coincident(g9,g10)
    c: Coincident(g10,g11)
    c: Coincident(g11,g8)
    c: Vertical(g8)
    c: Vertical(g10)
    c: Horizontal(g9)
    c: Horizontal(g11)
    c: Distance(g0,g4) = 2
    c: Distance(g1,g5) = 0.3
    c: DistanceX(g7,g7) = 14
    c: DistanceY(g4,g4) = 8
    c: Distance(g1,g9) = 9.15
    c: Distance(g0,g8) = 4.125
    c: DistanceX(g11,g11) = 6.2
    c: DistanceY(g10,g10) = 3
    c: Diameter(g12) = 4
    c: Equal(g12,g13)
    c: Equal(g13,g14)
    c: Distance(g12,g2) = 18.275
    c: Distance(g13,g2) = 18.275
    c: Distance(g14,g2) = 18.275
    c: Distance(g12,g3) = 18
    c: DistanceY(g13,g12) = 8
    c: DistanceY(g14,g13) = 8
FEATURE [PartDesign::Pocket] Pocket004  label="top_holes_p"
  BaseFeature = -> Pocket002
  Direction = (0,0,-1)
  Length = 5
  Length2 = 5
  Profile = -> Sketch009
  ReferenceAxis = -> Sketch009 [N_Axis]
  Refine = true
  Reversed = true
  Suppressed = false
  Type = 1
FEATURE [Sketcher::SketchObject] Sketch020  label="clips_s"
  ArcFitTolerance = 1e-06
  AttachmentSupport = -> [YZ_Plane002]
  ExternalGeometry = -> [Pocket004]
  FullyConstrained = true
  MakeInternals = false
  MapMode = 5
  Placement = pos=(0,0,0) rot=(0.57735,0.57735,0.57735;2.0944rad)
  sketch-geometry (12):
    g0: LineSegment StartX=35 StartY=7 StartZ=0 EndX=35 EndY=18 EndZ=0
    g1: LineSegment StartX=35 StartY=18 StartZ=0 EndX=34.5 EndY=18 EndZ=0
    g2: LineSegment StartX=34.5 StartY=18 StartZ=0 EndX=32 EndY=14.15 EndZ=0
    g3: LineSegment StartX=32 StartY=14.15 StartZ=0 EndX=33 EndY=14.15 EndZ=0
    g4: LineSegment StartX=33 StartY=14.15 StartZ=0 EndX=33 EndY=7 EndZ=0
    g5: LineSegment StartX=33 StartY=7 StartZ=0 EndX=35 EndY=7 EndZ=0
    g6: LineSegment StartX=-35 StartY=7 StartZ=0 EndX=-35 EndY=18 EndZ=0
    g7: LineSegment StartX=-35 StartY=18 StartZ=0 EndX=-34.5 EndY=18 EndZ=0
    g8: LineSegment StartX=-34.5 StartY=18 StartZ=0 EndX=-32 EndY=14.15 EndZ=0
    g9: LineSegment StartX=-32 StartY=14.15 StartZ=0 EndX=-33 EndY=14.15 EndZ=0
    g10: LineSegment StartX=-33 StartY=14.15 StartZ=0 EndX=-33 EndY=7 EndZ=0
    g11: LineSegment StartX=-33 StartY=7 StartZ=0 EndX=-35 EndY=7 EndZ=0
  constraints (34):
    c: Coincident(g-4,g0)
    c: Vertical(g0)
    c: Coincident(g0,g1)
    c: Coincident(g1,g2)
    c: Coincident(g2,g3)
    c: Horizontal(g3)
    c: Coincident(g3,g4)
    c: Vertical(g4)
    c: Coincident(g4,g5)
    c: Coincident(g5,g0)
    c: Horizontal(g5)
    c: DistanceY(g0,g0) = 11
    c: Horizontal(g1)
    c: DistanceX(g5,g5) = 2
    c: DistanceX(g1,g1) = 0.5
    c: DistanceX(g3,g3) = 1
    c: DistanceY(g4,g4) = 7.15
    c: Coincident(g-5,g6)
    c: Vertical(g6)
    c: Coincident(g6,g7)
    c: Horizontal(g7)
    c: Coincident(g7,g8)
    c: Coincident(g8,g9)
    c: Coincident(g9,g10)
    c: Coincident(g10,g11)
    c: Coincident(g11,g6)
    c: DistanceY(g6,g6) = 11
    c: Horizontal(g11)
    c: Horizontal(g9)
    c: Vertical(g10)
    c: DistanceY(g10,g10) = 7.15
    c: DistanceX(g7,g7) = 0.5
    c: DistanceX(g9,g9) = 1
    c: DistanceX(g11,g11) = 2
FEATURE [PartDesign::Pad] Pad010  label="clips_p"
  BaseFeature = -> Pocket004
  Direction = (1,0,0)
  Length = 9.45
  Length2 = 10
  Midplane = true
  Profile = -> Sketch020
  ReferenceAxis = -> Sketch020 [N_Axis]
  Refine = true
  Suppressed = false
  Type = 0
FEATURE [Sketcher::SketchObject] Sketch033
  ArcFitTolerance = 1e-06
  AttachmentSupport = -> [XY_Plane002]
  ExternalGeometry = -> [Pad010]
  FullyConstrained = true
  MakeInternals = false
  MapMode = 5
  sketch-geometry (13):
    g0: LineSegment [constr] StartX=-16 StartY=-19.7 StartZ=0 EndX=-16 EndY=-27.7 EndZ=0
    g1: LineSegment [constr] StartX=-16 StartY=-27.7 StartZ=0 EndX=-14 EndY=-27.7 EndZ=0
    g2: LineSegment [constr] StartX=-14 StartY=-27.7 StartZ=0 EndX=-14 EndY=-19.7 EndZ=0
    g3: LineSegment [constr] StartX=-14 StartY=-19.7 StartZ=0 EndX=-16 EndY=-19.7 EndZ=0
    g4: LineSegment StartX=-14 StartY=-19.7 StartZ=0 EndX=-14 EndY=-27.7 EndZ=0
    g5: LineSegment StartX=-14 StartY=-27.7 StartZ=0 EndX=-12 EndY=-27.7 EndZ=0
    g6: LineSegment StartX=-12 StartY=-27.7 StartZ=0 EndX=-12 EndY=-19.7 EndZ=0
    g7: LineSegment StartX=-12 StartY=-19.7 StartZ=0 EndX=-14 EndY=-19.7 EndZ=0
    g8: LineSegment [constr] StartX=-12 StartY=-19.7 StartZ=0 EndX=-6 EndY=-19.7 EndZ=0
    g9: LineSegment StartX=-6 StartY=-19.7 StartZ=0 EndX=-6 EndY=-27.7 EndZ=0
    g10: LineSegment StartX=-6 StartY=-27.7 StartZ=0 EndX=-4 EndY=-27.7 EndZ=0
    g11: LineSegment StartX=-4 StartY=-27.7 StartZ=0 EndX=-4 EndY=-19.7 EndZ=0
    g12: LineSegment StartX=-4 StartY=-19.7 StartZ=0 EndX=-6 EndY=-19.7 EndZ=0
  constraints (36):
    c: Coincident(g0,g1)
    c: Coincident(g1,g2)
    c: Coincident(g2,g3)
    c: Coincident(g3,g0)
    c: Vertical(g0)
    c: Vertical(g2)
    c: Horizontal(g1)
    c: Horizontal(g3)
    c: Distance(g0,g2) = 2
    c: Distance(g1,g3) = 8
    c: Coincident(g0,g-3)
    c: Coincident(g4,g5)
    c: Coincident(g5,g6)
    c: Coincident(g6,g7)
    c: Coincident(g7,g4)
    c: Vertical(g4)
    c: Vertical(g6)
    c: Horizontal(g5)
    c: Horizontal(g7)
    c: Distance(g4,g6) = 2
    c: Distance(g5,g7) = 8
    c: Coincident(g4,g2)
    c: Distance(g8) = 6
    c: Coincident(g8,g6)
    c: Horizontal(g8)
    c: Coincident(g9,g10)
    c: Coincident(g10,g11)
    c: Coincident(g11,g12)
    c: Coincident(g12,g9)
    c: Vertical(g9)
    c: Vertical(g11)
    c: Horizontal(g10)
    c: Horizontal(g12)
    c: Distance(g9,g11) = 2
    c: Distance(g10,g12) = 8
    c: Coincident(g9,g8)
FEATURE [PartDesign::Pad] Pad020  label="cable_clips_bottom"
  BaseFeature = -> Pad010
  Direction = (0,0,1)
  Length = 2
  Length2 = 10
  Profile = -> Sketch033
  ReferenceAxis = -> Sketch033 [N_Axis]
  Refine = true
  Reversed = true
  Suppressed = false
  Type = 0
FEATURE [PartDesign::Fillet] Fillet005  label="cable_clips_f"
  Base = -> Pad020 [Edge98,Edge82,Edge101,Edge85]
  BaseFeature = -> Pad020
  Radius = 1
  Refine = true
  SupportTransform = false
  Suppressed = false
  UseAllEdges = false
FEATURE [Sketcher::SketchObject] Sketch034
  ArcFitTolerance = 1e-06
  AttachmentOffset = pos=(0,0,-2) rot=(0,0,1;0rad)
  AttachmentSupport = -> [XY_Plane002]
  ExternalGeometry = -> [Sketch033]
  FullyConstrained = true
  MakeInternals = false
  MapMode = 5
  Placement = pos=(0,0,-2) rot=(0,0,1;0rad)
  sketch-geometry (5):
    g0: LineSegment [constr] StartX=-12 StartY=-19.7 StartZ=0 EndX=-10 EndY=-19.7 EndZ=0
    g1: LineSegment StartX=-10 StartY=-19.7 StartZ=0 EndX=-10 EndY=-27.7 EndZ=0
    g2: LineSegment StartX=-10 StartY=-27.7 StartZ=0 EndX=-8 EndY=-27.7 EndZ=0
    g3: LineSegment StartX=-8 StartY=-27.7 StartZ=0 EndX=-8 EndY=-19.7 EndZ=0
    g4: LineSegment StartX=-8 StartY=-19.7 StartZ=0 EndX=-10 EndY=-19.7 EndZ=0
  constraints (14):
    c: Distance(g0) = 2
    c: Coincident(g0,g-3)
    c: Horizontal(g0)
    c: Coincident(g1,g2)
    c: Coincident(g2,g3)
    c: Coincident(g3,g4)
    c: Coincident(g4,g1)
    c: Vertical(g1)
    c: Vertical(g3)
    c: Horizontal(g2)
    c: Horizontal(g4)
    c: Distance(g1,g3) = 2
    c: Distance(g2,g4) = 8
    c: Coincident(g1,g0)
FEATURE [Sketcher::SketchObject] Sketch035
  ArcFitTolerance = 1e-06
  AttachmentSupport = -> [XY_Plane002]
  ExternalGeometry = -> [Sketch033]
  FullyConstrained = true
  MakeInternals = false
  MapMode = 5
  sketch-geometry (5):
    g0: LineSegment [constr] StartX=-12 StartY=-19.7 StartZ=0 EndX=-10 EndY=-19.7 EndZ=0
    g1: LineSegment StartX=-10 StartY=-19.7 StartZ=0 EndX=-10 EndY=-21.7 EndZ=0
    g2: LineSegment StartX=-10 StartY=-21.7 StartZ=0 EndX=-8 EndY=-21.7 EndZ=0
    g3: LineSegment StartX=-8 StartY=-21.7 StartZ=0 EndX=-8 EndY=-19.7 EndZ=0
    g4: LineSegment StartX=-8 StartY=-19.7 StartZ=0 EndX=-10 EndY=-19.7 EndZ=0
  constraints (14):
    c: Distance(g0) = 2
    c: Coincident(g0,g-3)
    c: Horizontal(g0)
    c: Coincident(g1,g2)
    c: Coincident(g2,g3)
    c: Coincident(g3,g4)
    c: Coincident(g4,g1)
    c: Vertical(g1)
    c: Vertical(g3)
    c: Horizontal(g2)
    c: Horizontal(g4)
    c: Distance(g1,g3) = 2
    c: Distance(g2,g4) = 2
    c: Coincident(g1,g0)
FEATURE [PartDesign::Pad] Pad022  label="cable_clip_top_holder"
  BaseFeature = -> Fillet005
  Direction = (0,0,1)
  Length = 2.5
  Length2 = 10
  Profile = -> Sketch035
  ReferenceAxis = -> Sketch035 [N_Axis]
  Refine = true
  Reversed = true
  Suppressed = false
  Type = 0
FEATURE [PartDesign::Pad] Pad023  label="cable_clip_top"
  BaseFeature = -> Pad022
  Direction = (0,0,1)
  Length = 2
  Length2 = 10
  Profile = -> Sketch034
  ReferenceAxis = -> Sketch034 [N_Axis]
  Refine = true
  Reversed = true
  Suppressed = false
  Type = 0
FEATURE [PartDesign::Fillet] Fillet006
  Base = -> Pad023 [Edge177,Edge174,Edge148]
  BaseFeature = -> Pad023
  Radius = 0.9
  Refine = true
  SupportTransform = false
  Suppressed = false
  UseAllEdges = false
FEATURE [PartDesign::Body] Body001  label="top_b"
  AllowCompound = false
  Group = -> [Sketch005,Pad003,Thickness001,Fillet002,Sketch008,Pocket002,Sketch009,Pocket004,Sketch020,Pad010,Sketch033,Pad020,Fillet005,Sketch034,Sketch035,Pad022,Pad023,Fillet006]
  Origin = -> Origin002
  Placement = pos=(90,0,0) rot=(0,0,1;0rad)
  Tip = -> Fillet006
PROVENANCE & LICENSES
A FreeCAD (.FCStd) document from a public repository crawl; recipes are the document's own serialized feature recipes (and, for linked parts, companion documents' recipes).
License: as declared in the source repository (recorded in the dataset sidecar).
